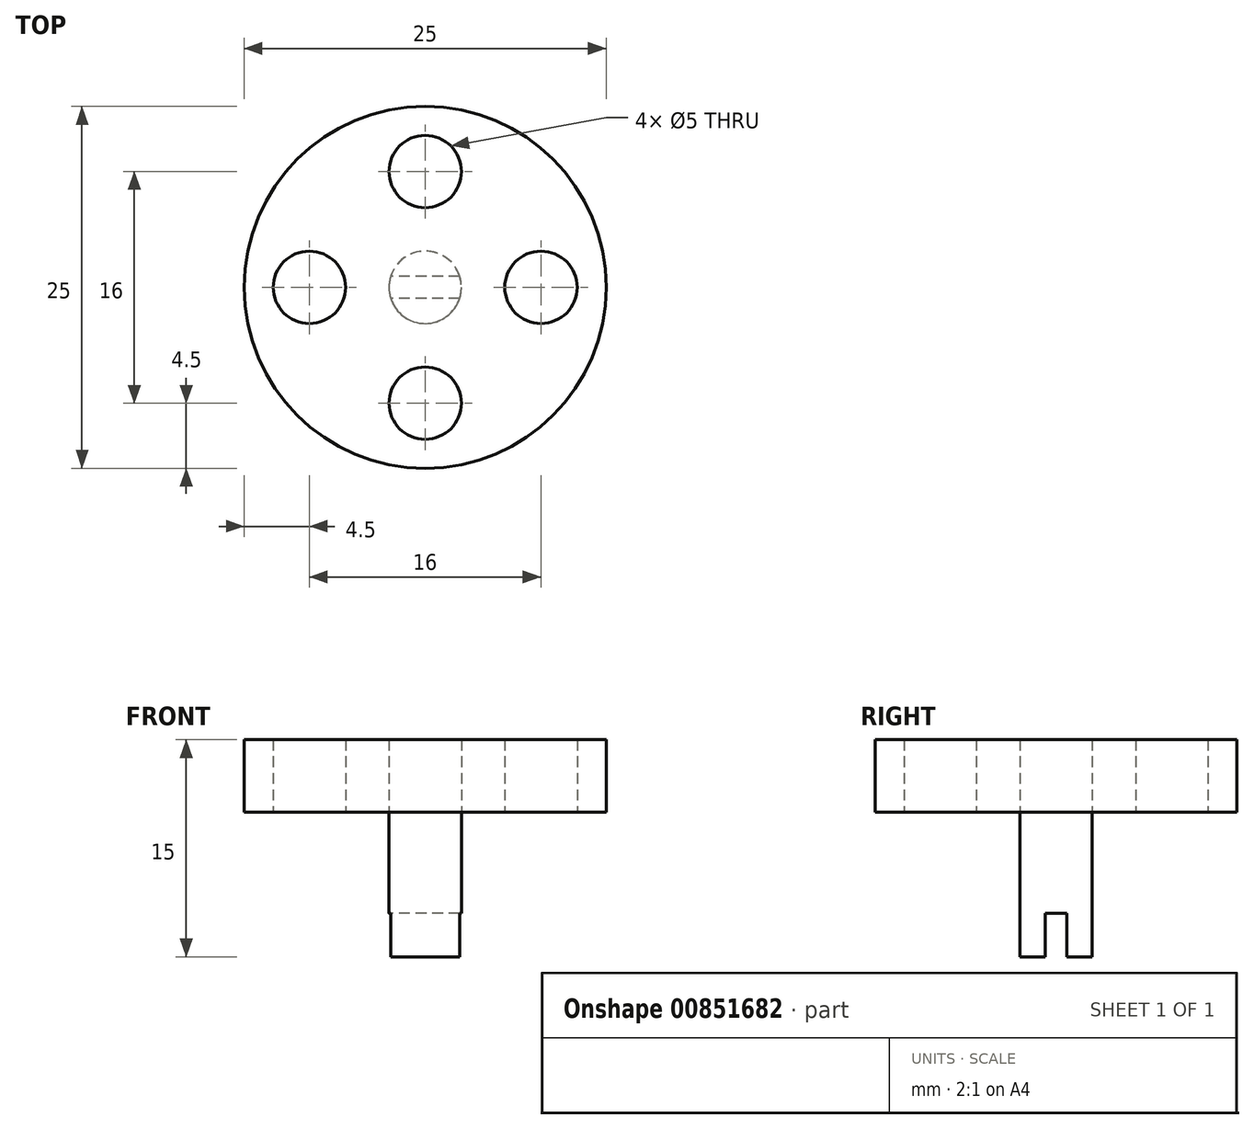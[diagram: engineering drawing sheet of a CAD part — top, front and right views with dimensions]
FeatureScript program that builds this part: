
annotation { "Feature Type Name" : "Feature", "Feature Type Description" : "" }
export const myFeature = defineFeature(function(context is Context, id is Id, definition is map)
    precondition{}
    {
        {
            var Q0;
            Q0=qCreatedBy(makeId("Top.planeOp"),FACE);
            var sketch = newSketch(context, id + "F0", { "sketchPlane" : qUnion([Q0])});
            skCircle(sketch, "E0", {"center": v(0, 0) * mm, "radius": 12.5 * mm});
            skLineSegment(sketch, "E1", {"start": v(0, 0) * mm, "end": v(0, 8) * mm, "construction": true});
            skCircle(sketch, "E2", {"center": v(0, 8) * mm, "radius": 2.5 * mm});
            skLineSegment(sketch, "E3", {"start": v(0, 0) * mm, "end": v(-8, 0) * mm, "construction": true});
            skCircle(sketch, "E4", {"center": v(-8, 0) * mm, "radius": 2.5 * mm});
            skCircle(sketch, "E5.MirrorC", {"center": v(8, 0) * mm, "radius": 2.5 * mm});
            skCircle(sketch, "E6.MirrorC", {"center": v(0, -8) * mm, "radius": 2.5 * mm});
            skSolve(sketch);
        }
        {
            var Q0;
            Q0=makeQuery(id+"F0.imprint","IMPRINT",FACE,{"disambiguationData":[TD([[makeQuery(id+"F0.imprint","IMPRINT",EDGE,{"derivedFrom":sQuery(id+"F0.wireOp",EDGE,"E0")}),1.0]])]});
            extrude(context, id + "F1", {"entities" : qUnion([Q0]), "depth" : 5 * mm, "offsetDistance" : 25 * mm});
        }
        {
            var Q0;
            Q0=makeQuery(id+"F1.opExtrude","CAP_FACE",FACE,{"disambiguationData":[OSD([sQuery(id+"F0.wireOp",EDGE,"E0"),sQuery(id+"F0.wireOp",EDGE,"E2"),sQuery(id+"F0.wireOp",EDGE,"E4")])],"isStart":true});
            var sketch = newSketch(context, id + "F2", { "sketchPlane" : qUnion([Q0])});
            skCircle(sketch, "E7", {"center": v(0, 0) * mm, "radius": 2.5 * mm});
            skSolve(sketch);
        }
        {
            var Q0;
            Q0=makeQuery(id+"F2.imprint","IMPRINT",FACE,{"disambiguationData":[TD([[makeQuery(id+"F2.imprint","IMPRINT",EDGE,{"derivedFrom":sQuery(id+"F2.wireOp",EDGE,"E7")}),1.0]])]});
            extrude(context, id + "F3", {"entities" : qUnion([Q0]), "oppositeDirection" : true, "depth" : -10 * mm, "offsetDistance" : 25 * mm});
        }
        {
            var Q0;
            Q0=makeQuery(id+"F3.opExtrude","CAP_FACE",FACE,{"disambiguationData":[OSD([sQuery(id+"F2.wireOp",EDGE,"E7")])],"isStart":false});
            var sketch = newSketch(context, id + "F4", { "sketchPlane" : qUnion([Q0])});
            skLineSegment(sketch, "E8.bottom", {"start": v(3.84, 0.75) * mm, "end": v(-3.84, 0.75) * mm});
            skLineSegment(sketch, "E8.top", {"start": v(3.84, -0.75) * mm, "end": v(-3.84, -0.75) * mm});
            skLineSegment(sketch, "E8.left", {"start": v(3.84, 0.75) * mm, "end": v(3.84, -0.75) * mm});
            skLineSegment(sketch, "E8.right", {"start": v(-3.84, 0.75) * mm, "end": v(-3.84, -0.75) * mm});
            skPoint(sketch, "E8.middle", {"position": v(0, 0) * mm});
            skSolve(sketch);
        }
        {
            var Q0;
            {var subQ0=sQuery(id+"F4.wireOp",EDGE,"E8.bottom");var subQ1=makeQuery(id+"F3.opExtrude","CAP_EDGE",EDGE,{"disambiguationData":[OSD([sQuery(id+"F2.wireOp",EDGE,"E7")])],"isStart":false});var subQ2=makeQuery(id+"F4.imprint","INTERSECT",VERTEX,{"disambiguationData":[OD(0.0)],"derivedFrom":[subQ1,subQ0]});Q0=makeQuery(id+"F4.imprint","IMPRINT",FACE,{"disambiguationData":[TD([[makeQuery(id+"F4.imprint","IMPRINT",EDGE,{"disambiguationData":[TD([[subQ2,-1.0]])],"derivedFrom":subQ0}),1.0]])]});}
            extrude(context, id + "F5", {"entities" : qUnion([Q0]), "operationType" : NewBodyOperationType.REMOVE, "oppositeDirection" : true, "depth" : 3 * mm, "offsetDistance" : 25 * mm});
        }
    });
